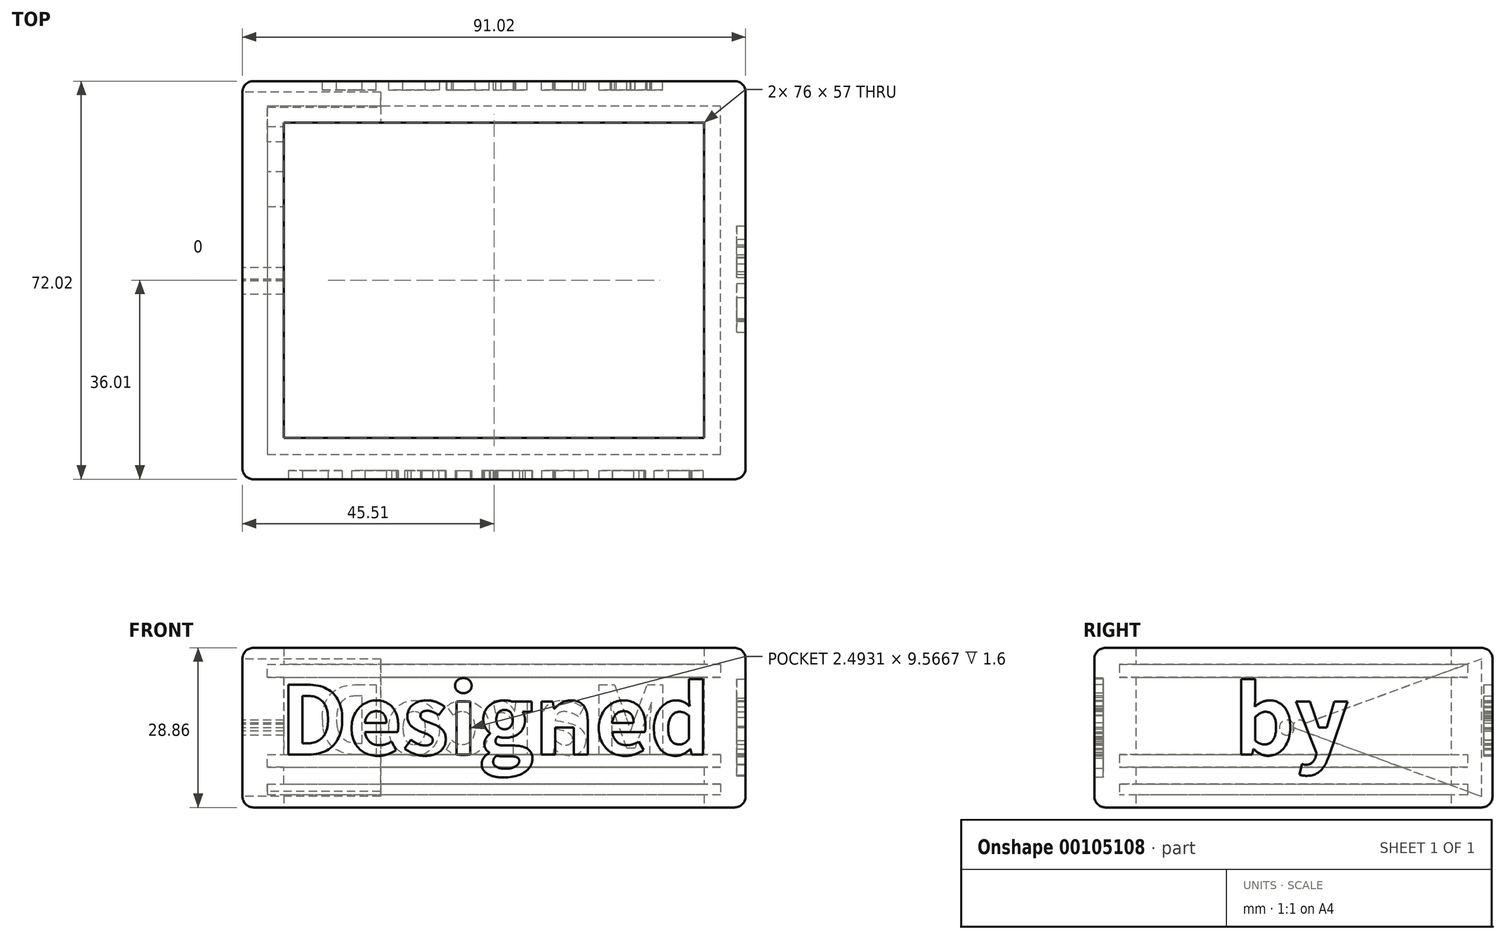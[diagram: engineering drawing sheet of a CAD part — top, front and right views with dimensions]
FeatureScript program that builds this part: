
annotation { "Feature Type Name" : "Feature", "Feature Type Description" : "" }
export const myFeature = defineFeature(function(context is Context, id is Id, definition is map)
    precondition{}
    {
        {
            var Q0;
            Q0=qCreatedBy(makeId("Top.planeOp"),FACE);
            var sketch = newSketch(context, id + "F0", { "sketchPlane" : qUnion([Q0])});
            skPoint(sketch, "E0.middle", {"position": v(0, 0) * mm});
            skLineSegment(sketch, "E1.bottom", {"start": v(0, 0) * mm, "end": v(82, 0) * mm});
            skLineSegment(sketch, "E1.top", {"start": v(0, -63) * mm, "end": v(82, -63) * mm});
            skLineSegment(sketch, "E1.left", {"start": v(0, 0) * mm, "end": v(0, -63) * mm});
            skLineSegment(sketch, "E1.right", {"start": v(82, 0) * mm, "end": v(82, -63) * mm});
            skSolve(sketch);
        }
        {
            var Q0;
            Q0=qCreatedBy(makeId("Front.planeOp"),FACE);
            var sketch = newSketch(context, id + "F1", { "sketchPlane" : qUnion([Q0])});
            skLineSegment(sketch, "E2", {"start": v(3, -5.3) * mm, "end": v(0, -5.3) * mm});
            skLineSegment(sketch, "E3", {"start": v(0, -5.3) * mm, "end": v(0, -7.3) * mm});
            skLineSegment(sketch, "E4", {"start": v(0, -7.3) * mm, "end": v(3, -7.3) * mm});
            skLineSegment(sketch, "E5", {"start": v(3, 0) * mm, "end": v(0, 0) * mm});
            skLineSegment(sketch, "E6", {"start": v(0, 0) * mm, "end": v(0, -2.3) * mm});
            skLineSegment(sketch, "E7", {"start": v(0, -2.3) * mm, "end": v(3, -2.3) * mm});
            skLineSegment(sketch, "E8", {"start": v(3, 14) * mm, "end": v(0, 14) * mm});
            skLineSegment(sketch, "E9", {"start": v(0, 14) * mm, "end": v(0, 16.3) * mm});
            skLineSegment(sketch, "E10", {"start": v(0, 16.3) * mm, "end": v(3, 16.3) * mm});
            skLineSegment(sketch, "E11", {"start": v(3, 16.3) * mm, "end": v(3, 19.3) * mm});
            skLineSegment(sketch, "E12", {"start": v(3, 19.3) * mm, "end": v(-4.51, 19.3) * mm});
            skLineSegment(sketch, "E13", {"start": v(3, -7.3) * mm, "end": v(3, -9.56) * mm});
            skLineSegment(sketch, "E14", {"start": v(3, -9.56) * mm, "end": v(-4.51, -9.56) * mm});
            skLineSegment(sketch, "E15", {"start": v(3, 14) * mm, "end": v(3, 0) * mm});
            skLineSegment(sketch, "E16", {"start": v(3, -2.3) * mm, "end": v(3, -5.3) * mm});
            skLineSegment(sketch, "E17", {"start": v(-4.51, 19.3) * mm, "end": v(-4.51, -9.56) * mm});
            skSolve(sketch);
        }
        {
            var Q0;
            Q0 = qSketchRegion(id + "F1", true);
            var Q1;
            Q1 = qConstructionFilter(qBodyType(qCreatedBy(id + "F0" ,EDGE), BodyType.WIRE), ConstructionObject.NO);
            sweep(context, id + "F2", {"profiles" : qUnion([Q0]), "path" : qUnion([Q1])});
        }
        {
            var Q0;
            Q0=makeQuery(id+"F2.opSweep","MID_CAP_EDGE",EDGE,{"disambiguationData":[OSD([sQuery(id+"F0.wireOp",VERTEX,"E1.left.end"),sQuery(id+"F1.wireOp",EDGE,"E17")])],"capPos":1.0});
            var Q1;
            Q1=makeQuery(id+"F2.opSweep","SWEPT_EDGE",EDGE,{"disambiguationData":[OSD([sQuery(id+"F0.wireOp",EDGE,"E1.top"),sQuery(id+"F1.wireOp",EDGE,"E12"),sQuery(id+"F1.wireOp",EDGE,"E17")])]});
            var Q2;
            Q2=makeQuery(id+"F2.opSweep","SWEPT_EDGE",EDGE,{"disambiguationData":[OSD([sQuery(id+"F0.wireOp",EDGE,"E1.left"),sQuery(id+"F1.wireOp",EDGE,"E12"),sQuery(id+"F1.wireOp",EDGE,"E17")])]});
            var Q3;
            Q3=makeQuery(id+"F2.opSweep","SWEPT_FACE",FACE,{"disambiguationData":[OSD([sQuery(id+"F0.wireOp",EDGE,"E1.left"),sQuery(id+"F1.wireOp",EDGE,"E17")])]});
            var Q4;
            Q4=makeQuery(id+"F2.opSweep","SWEPT_FACE",FACE,{"disambiguationData":[OSD([sQuery(id+"F0.wireOp",EDGE,"E1.top"),sQuery(id+"F1.wireOp",EDGE,"E17")])]});
            var Q5;
            Q5=makeQuery(id+"F2.opSweep","SWEPT_FACE",FACE,{"disambiguationData":[OSD([sQuery(id+"F0.wireOp",EDGE,"E1.bottom"),sQuery(id+"F1.wireOp",EDGE,"E17")])]});
            var Q6;
            Q6=makeQuery(id+"F2.opSweep","SWEPT_FACE",FACE,{"disambiguationData":[OSD([sQuery(id+"F0.wireOp",EDGE,"E1.right"),sQuery(id+"F1.wireOp",EDGE,"E17")])]});
            fillet(context, id + "F3", {"entities" : qUnion([Q0, Q1, Q2, Q3, Q4, Q5, Q6]), "radius" : 2 * mm, "tangentPropagation" : true, "allowEdgeOverflow" : false});
        }
        {
            var Q0;
            Q0=makeQuery(id+"F2.opSweep","SWEPT_FACE",FACE,{"disambiguationData":[OSD([sQuery(id+"F0.wireOp",EDGE,"E1.top"),sQuery(id+"F1.wireOp",EDGE,"E17")])]});
            var sketch = newSketch(context, id + "F4", { "sketchPlane" : qUnion([Q0])});
            skText(sketch, "E18", { "text": "Designed", "fontName": "NotoSansCJKsc-Bold.otf"});
            skLineSegment(sketch, "E19", {"start": v(41, 17.3) * mm, "end": v(41, -7.56) * mm});
            skLineSegment(sketch, "E20", {"start": v(41, 4.87) * mm, "end": v(84.51, 4.87) * mm});
            const initialGuessF4  = {"E18": [0.00227, 0, 1, 0, 0.0123]};
            skSetInitialGuess(sketch, initialGuessF4);
            skSolve(sketch);
        }
        {
            var Q0;
            Q0 = qSketchRegion(id + "F4", true);
            extrude(context, id + "F5", {"entities" : qUnion([Q0]), "operationType" : NewBodyOperationType.REMOVE, "oppositeDirection" : true, "depth" : 1.6 * mm});
        }
        {
            var Q0;
            Q0=makeQuery(id+"F2.opSweep","SWEPT_FACE",FACE,{"disambiguationData":[OSD([sQuery(id+"F0.wireOp",EDGE,"E1.right"),sQuery(id+"F1.wireOp",EDGE,"E17")])]});
            var sketch = newSketch(context, id + "F6", { "sketchPlane" : qUnion([Q0])});
            skText(sketch, "E21", { "text": "by", "fontName": "NotoSansCJKsc-Bold.otf"});
            skLineSegment(sketch, "E22", {"start": v(-31.5, 17.3) * mm, "end": v(-31.5, -7.56) * mm});
            skLineSegment(sketch, "E23", {"start": v(-65.51, 4.87) * mm, "end": v(2.51, 4.87) * mm});
            const initialGuessF6  = {"E21": [-0.04228, 0, 1, 0, 0.0123]};
            skSetInitialGuess(sketch, initialGuessF6);
            skSolve(sketch);
        }
        {
            var Q0;
            Q0 = qSketchRegion(id + "F6", true);
            extrude(context, id + "F7", {"entities" : qUnion([Q0]), "operationType" : NewBodyOperationType.REMOVE, "oppositeDirection" : true, "depth" : 1.6 * mm});
        }
        {
            var Q0;
            Q0=makeQuery(id+"F2.opSweep","SWEPT_FACE",FACE,{"disambiguationData":[OSD([sQuery(id+"F0.wireOp",EDGE,"E1.bottom"),sQuery(id+"F1.wireOp",EDGE,"E17")])]});
            var sketch = newSketch(context, id + "F8", { "sketchPlane" : qUnion([Q0])});
            skText(sketch, "E24", { "text": "MarcoD", "fontName": "NotoSansCJKsc-Bold.otf"});
            skLineSegment(sketch, "E25", {"start": v(-41, 17.3) * mm, "end": v(-41, -7.56) * mm});
            skLineSegment(sketch, "E26", {"start": v(2.51, 4.87) * mm, "end": v(-41, 4.87) * mm});
            const initialGuessF8  = {"E24": [-0.07304, 0, 1, 0, 0.0123]};
            skSetInitialGuess(sketch, initialGuessF8);
            skSolve(sketch);
        }
        {
            var Q0;
            Q0 = qSketchRegion(id + "F8", true);
            extrude(context, id + "F9", {"entities" : qUnion([Q0]), "operationType" : NewBodyOperationType.REMOVE, "oppositeDirection" : true, "depth" : 1.6 * mm});
        }
        {
            var Q0;
            Q0=makeQuery(id+"F2.opSweep","SWEPT_FACE",FACE,{"disambiguationData":[OSD([sQuery(id+"F0.wireOp",EDGE,"E1.left"),sQuery(id+"F1.wireOp",EDGE,"E17")])]});
            var sketch = newSketch(context, id + "F10", { "sketchPlane" : qUnion([Q0])});
            skLineSegment(sketch, "E27", {"start": v(-2.51, 17.3) * mm, "end": v(65.51, -7.56) * mm});
            skLineSegment(sketch, "E28", {"start": v(65.51, 17.3) * mm, "end": v(-2.51, -7.56) * mm});
            skLineSegment(sketch, "E29", {"start": v(31.5, 17.3) * mm, "end": v(31.5, 4.87) * mm});
            skCircle(sketch, "E30", {"center": v(32.7, 4.87) * mm, "radius": 1.35 * mm});
            skLineSegment(sketch, "E31", {"start": v(31.5, 4.87) * mm, "end": v(31.5, -7.56) * mm});
            skCircle(sketch, "E32.MirrorC", {"center": v(30.3, 4.87) * mm, "radius": 1.35 * mm});
            skSolve(sketch);
        }
        {
            var Q0;
            {var subQ1=sQuery(id+"F10.wireOp",EDGE,"E28");var subQ3=sQuery(id+"F10.wireOp",EDGE,"E30");var subQ4=makeQuery(id+"F10.imprint","INTERSECT",VERTEX,{"disambiguationData":[OD(0.0)],"derivedFrom":[subQ1,subQ3]});Q0=makeQuery(id+"F10.imprint","IMPRINT",FACE,{"disambiguationData":[TD([[makeQuery(id+"F10.imprint","IMPRINT",EDGE,{"disambiguationData":[TD([[subQ4,-1.0]])],"derivedFrom":subQ3}),1.0]])]});}
            var Q1;
            {var subQ1=sQuery(id+"F10.wireOp",EDGE,"E27");var subQ3=sQuery(id+"F10.wireOp",EDGE,"E30");var subQ4=makeQuery(id+"F10.imprint","INTERSECT",VERTEX,{"disambiguationData":[OD(1.0)],"derivedFrom":[subQ1,subQ3]});Q1=makeQuery(id+"F10.imprint","IMPRINT",FACE,{"disambiguationData":[TD([[makeQuery(id+"F10.imprint","IMPRINT",EDGE,{"disambiguationData":[TD([[subQ4,-1.0]])],"derivedFrom":subQ3}),1.0]])]});}
            var Q2;
            {var subQ1=sQuery(id+"F10.wireOp",EDGE,"E27");var subQ3=sQuery(id+"F10.wireOp",EDGE,"E30");var subQ4=makeQuery(id+"F10.imprint","INTERSECT",VERTEX,{"disambiguationData":[OD(1.0)],"derivedFrom":[subQ1,subQ3]});Q2=makeQuery(id+"F10.imprint","IMPRINT",FACE,{"disambiguationData":[TD([[makeQuery(id+"F10.imprint","IMPRINT",EDGE,{"disambiguationData":[TD([[subQ4,1.0]])],"derivedFrom":subQ3}),1.0]])]});}
            var Q3;
            {var subQ0=sQuery(id+"F10.wireOp",EDGE,"E32.MirrorC");var subQ1=sQuery(id+"F10.wireOp",EDGE,"E27");var subQ2=makeQuery(id+"F10.imprint","INTERSECT",VERTEX,{"disambiguationData":[OD(0.0)],"derivedFrom":[subQ1,subQ0]});Q3=makeQuery(id+"F10.imprint","IMPRINT",FACE,{"disambiguationData":[TD([[makeQuery(id+"F10.imprint","IMPRINT",EDGE,{"disambiguationData":[TD([[subQ2,-1.0]])],"derivedFrom":subQ1}),-1.0]])]});}
            var Q4;
            {var subQ0=sQuery(id+"F10.wireOp",EDGE,"E32.MirrorC");var subQ1=sQuery(id+"F10.wireOp",EDGE,"E27");var subQ2=makeQuery(id+"F10.imprint","INTERSECT",VERTEX,{"disambiguationData":[OD(0.0)],"derivedFrom":[subQ1,subQ0]});Q4=makeQuery(id+"F10.imprint","IMPRINT",FACE,{"disambiguationData":[TD([[makeQuery(id+"F10.imprint","IMPRINT",EDGE,{"disambiguationData":[TD([[subQ2,-1.0]])],"derivedFrom":subQ1}),1.0]])]});}
            var Q5;
            {var subQ0=sQuery(id+"F10.wireOp",EDGE,"E30");var subQ1=sQuery(id+"F10.wireOp",EDGE,"E28");var subQ2=makeQuery(id+"F10.imprint","INTERSECT",VERTEX,{"disambiguationData":[OD(1.0)],"derivedFrom":[subQ1,subQ0]});Q5=makeQuery(id+"F10.imprint","IMPRINT",FACE,{"disambiguationData":[TD([[makeQuery(id+"F10.imprint","IMPRINT",EDGE,{"disambiguationData":[TD([[subQ2,-1.0]])],"derivedFrom":subQ1}),1.0]])]});}
            var Q6;
            {var subQ1=sQuery(id+"F10.wireOp",EDGE,"E27");var subQ3=sQuery(id+"F10.wireOp",EDGE,"E30");var subQ4=makeQuery(id+"F10.imprint","INTERSECT",VERTEX,{"disambiguationData":[OD(0.0)],"derivedFrom":[subQ1,subQ3]});Q6=makeQuery(id+"F10.imprint","IMPRINT",FACE,{"disambiguationData":[TD([[makeQuery(id+"F10.imprint","IMPRINT",EDGE,{"disambiguationData":[TD([[subQ4,1.0]])],"derivedFrom":subQ3}),1.0]])]});}
            var Q7;
            {var subQ1=sQuery(id+"F10.wireOp",EDGE,"E28");var subQ3=sQuery(id+"F10.wireOp",EDGE,"E32.MirrorC");var subQ4=makeQuery(id+"F10.imprint","INTERSECT",VERTEX,{"disambiguationData":[OD(0.0)],"derivedFrom":[subQ1,subQ3]});Q7=makeQuery(id+"F10.imprint","IMPRINT",FACE,{"disambiguationData":[TD([[makeQuery(id+"F10.imprint","IMPRINT",EDGE,{"disambiguationData":[TD([[subQ4,1.0]])],"derivedFrom":subQ3}),-1.0]])]});}
            var Q8;
            {var subQ1=sQuery(id+"F10.wireOp",EDGE,"E27");var subQ3=sQuery(id+"F10.wireOp",EDGE,"E32.MirrorC");var subQ4=makeQuery(id+"F10.imprint","INTERSECT",VERTEX,{"disambiguationData":[OD(1.0)],"derivedFrom":[subQ1,subQ3]});Q8=makeQuery(id+"F10.imprint","IMPRINT",FACE,{"disambiguationData":[TD([[makeQuery(id+"F10.imprint","IMPRINT",EDGE,{"disambiguationData":[TD([[subQ4,1.0]])],"derivedFrom":subQ3}),-1.0]])]});}
            var Q9;
            {var subQ1=sQuery(id+"F10.wireOp",EDGE,"E27");var subQ3=sQuery(id+"F10.wireOp",EDGE,"E32.MirrorC");var subQ4=makeQuery(id+"F10.imprint","INTERSECT",VERTEX,{"disambiguationData":[OD(1.0)],"derivedFrom":[subQ1,subQ3]});Q9=makeQuery(id+"F10.imprint","IMPRINT",FACE,{"disambiguationData":[TD([[makeQuery(id+"F10.imprint","IMPRINT",EDGE,{"disambiguationData":[TD([[subQ4,-1.0]])],"derivedFrom":subQ3}),-1.0]])]});}
            var Q10;
            {var subQ1=sQuery(id+"F10.wireOp",EDGE,"E28");var subQ3=sQuery(id+"F10.wireOp",EDGE,"E30");var subQ4=makeQuery(id+"F10.imprint","INTERSECT",VERTEX,{"disambiguationData":[OD(1.0)],"derivedFrom":[subQ1,subQ3]});Q10=makeQuery(id+"F10.imprint","IMPRINT",FACE,{"disambiguationData":[TD([[makeQuery(id+"F10.imprint","IMPRINT",EDGE,{"disambiguationData":[TD([[subQ4,-1.0]])],"derivedFrom":subQ3}),1.0]])]});}
            var Q11;
            {var subQ1=sQuery(id+"F10.wireOp",EDGE,"E27");var subQ3=sQuery(id+"F10.wireOp",EDGE,"E30");var subQ4=makeQuery(id+"F10.imprint","INTERSECT",VERTEX,{"disambiguationData":[OD(0.0)],"derivedFrom":[subQ1,subQ3]});Q11=makeQuery(id+"F10.imprint","IMPRINT",FACE,{"disambiguationData":[TD([[makeQuery(id+"F10.imprint","IMPRINT",EDGE,{"disambiguationData":[TD([[subQ4,-1.0]])],"derivedFrom":subQ3}),1.0]])]});}
            extrude(context, id + "F11", {"entities" : qUnion([Q0, Q1, Q2, Q3, Q4, Q5, Q6, Q7, Q8, Q9, Q10, Q11]), "operationType" : NewBodyOperationType.REMOVE, "oppositeDirection" : true, "depth" : 25 * mm});
        }
    });
